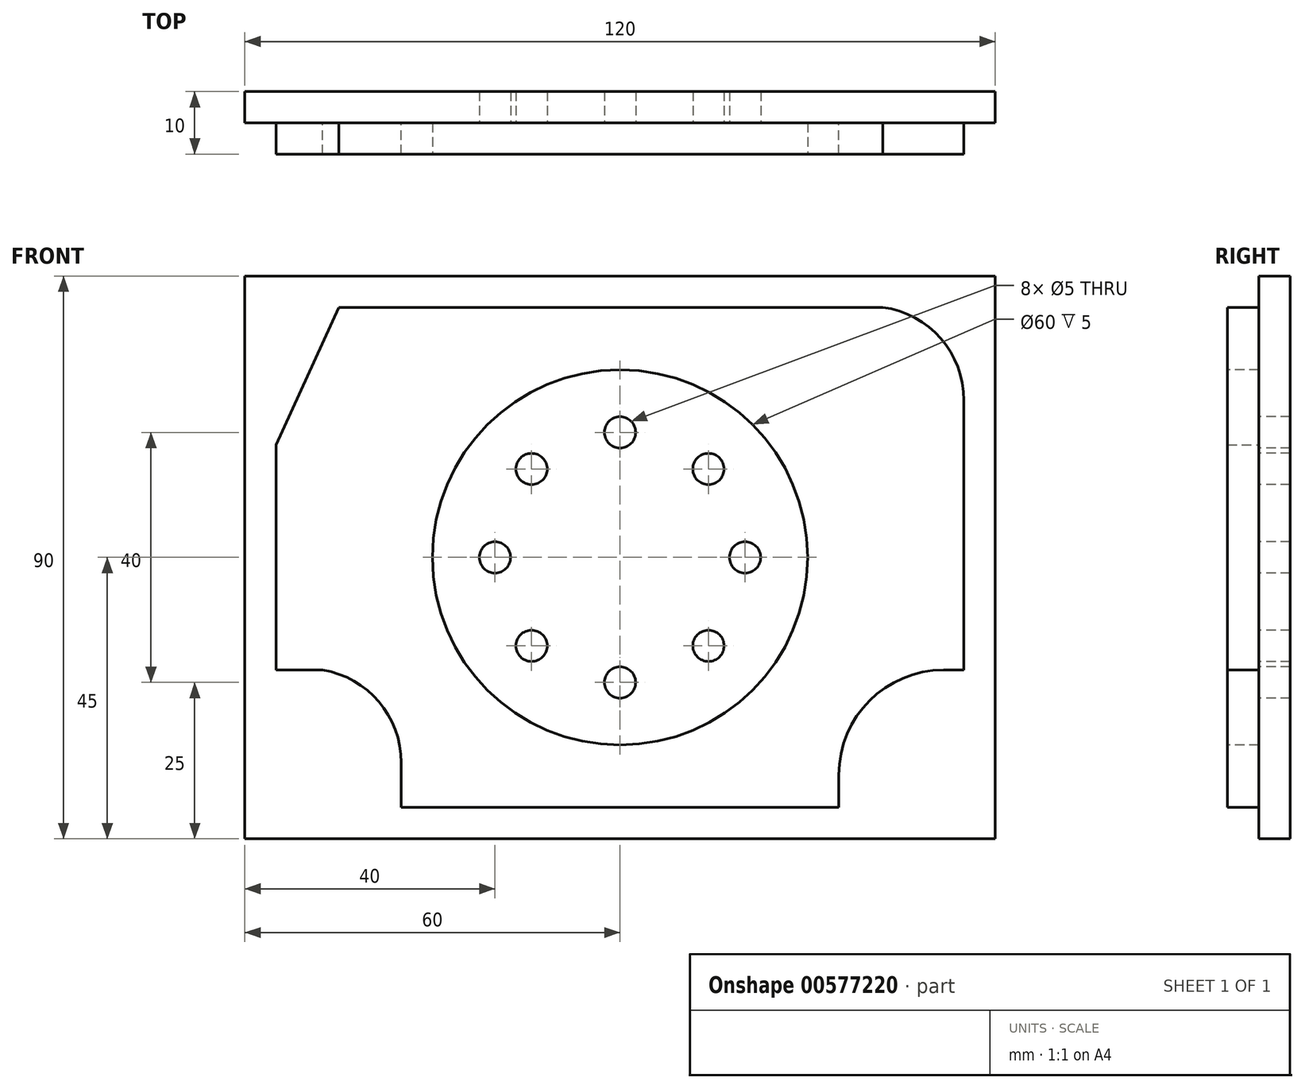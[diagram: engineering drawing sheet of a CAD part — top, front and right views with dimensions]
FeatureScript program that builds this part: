
annotation { "Feature Type Name" : "Feature", "Feature Type Description" : "" }
export const myFeature = defineFeature(function(context is Context, id is Id, definition is map)
    precondition{}
    {
        {
            var Q0;
            Q0=qCreatedBy(makeId("Front.planeOp"),FACE);
            var sketch = newSketch(context, id + "F0", { "sketchPlane" : qUnion([Q0])});
            skLineSegment(sketch, "E0.bottom", {"start": v(0, 0) * mm, "end": v(-120, 0) * mm});
            skLineSegment(sketch, "E0.top", {"start": v(0, 90) * mm, "end": v(-120, 90) * mm});
            skLineSegment(sketch, "E0.left", {"start": v(0, 0) * mm, "end": v(0, 90) * mm});
            skLineSegment(sketch, "E0.right", {"start": v(-120, 0) * mm, "end": v(-120, 90) * mm});
            skSolve(sketch);
        }
        {
            var Q0;
            Q0=makeQuery(id+"F0.imprint","IMPRINT",FACE,{"disambiguationData":[TD([[makeQuery(id+"F0.imprint","IMPRINT",EDGE,{"derivedFrom":sQuery(id+"F0.wireOp",EDGE,"E0.bottom")}),-1.0]])]});
            extrude(context, id + "F1", {"entities" : qUnion([Q0]), "depth" : 5 * mm, "offsetDistance" : 25 * mm});
        }
        {
            var Q0;
            Q0=makeQuery(id+"F1.opExtrude","CAP_FACE",FACE,{"disambiguationData":[OSD([sQuery(id+"F0.wireOp",EDGE,"E0.bottom"),sQuery(id+"F0.wireOp",EDGE,"E0.top"),sQuery(id+"F0.wireOp",EDGE,"E0.left"),sQuery(id+"F0.wireOp",EDGE,"E0.right")])],"isStart":false});
            var sketch = newSketch(context, id + "F2", { "sketchPlane" : qUnion([Q0])});
            skCircle(sketch, "E1", {"center": v(-60, 45) * mm, "radius": 20 * mm, "construction": true});
            skCircle(sketch, "E2", {"center": v(-60, 65) * mm, "radius": 3 * mm});
            skCircle(sketch, "E3", {"center": v(-60, 25) * mm, "radius": 3 * mm});
            skCircle(sketch, "E4", {"center": v(-45.86, 59.14) * mm, "radius": 3 * mm});
            skCircle(sketch, "E5", {"center": v(-45.86, 30.86) * mm, "radius": 3 * mm});
            skCircle(sketch, "E6", {"center": v(-74.14, 30.86) * mm, "radius": 3 * mm});
            skCircle(sketch, "E7", {"center": v(-74.14, 59.14) * mm, "radius": 3 * mm});
            skCircle(sketch, "E8", {"center": v(-80, 45) * mm, "radius": 3 * mm});
            skCircle(sketch, "E9", {"center": v(-40, 45) * mm, "radius": 3 * mm});
            skSolve(sketch);
        }
        {
            var Q0;
            Q0=sQuery(id+"F2.wireOp",VERTEX,"E7.center");
            var Q1;
            Q1=sQuery(id+"F2.wireOp",VERTEX,"E2.center");
            var Q2;
            Q2=sQuery(id+"F2.wireOp",VERTEX,"E4.center");
            var Q3;
            Q3=sQuery(id+"F2.wireOp",VERTEX,"E9.center");
            var Q4;
            Q4=sQuery(id+"F2.wireOp",VERTEX,"E5.center");
            var Q5;
            Q5=sQuery(id+"F2.wireOp",VERTEX,"E3.center");
            var Q6;
            Q6=sQuery(id+"F2.wireOp",VERTEX,"E8.center");
            var Q7;
            Q7=sQuery(id+"F2.wireOp",VERTEX,"E6.center");
            var Q8;
            Q8=makeQuery(id+"F1.opExtrude","SWEPT_BODY",BODY,{"disambiguationData":[OSD([sQuery(id+"F0.wireOp",EDGE,"E0.bottom"),sQuery(id+"F0.wireOp",EDGE,"E0.top"),sQuery(id+"F0.wireOp",EDGE,"E0.left"),sQuery(id+"F0.wireOp",EDGE,"E0.right")])]});
            hole(context, id + "F3", {"style" : HoleStyle.SIMPLE, "endStyle" : HoleEndStyle.THROUGH, "holeDiameter" : 5 * mm, "isTappedThrough" : true, "tappedDepth" : 12 * mm, "tapClearance" : 3, "locations" : qUnion([Q0, Q1, Q2, Q3, Q4, Q5, Q6, Q7]), "scope" : qUnion([Q8])});
        }
        {
            var Q0;
            Q0=makeQuery(id+"F1.opExtrude","CAP_FACE",FACE,{"disambiguationData":[OSD([sQuery(id+"F0.wireOp",EDGE,"E0.bottom"),sQuery(id+"F0.wireOp",EDGE,"E0.top"),sQuery(id+"F0.wireOp",EDGE,"E0.left"),sQuery(id+"F0.wireOp",EDGE,"E0.right")])],"isStart":false});
            var sketch = newSketch(context, id + "F4", { "sketchPlane" : qUnion([Q0])});
            skLineSegment(sketch, "E10", {"start": v(-5, 70.14) * mm, "end": v(-5, 27) * mm});
            skArc(sketch, "E11", {"start": v(-5, 70.14) * mm, "mid": v(-8.7, 80) * mm, "end": v(-17.99, 85) * mm});
            skLineSegment(sketch, "E12", {"start": v(-95, 5) * mm, "end": v(-25, 5) * mm});
            skLineSegment(sketch, "E13", {"start": v(-5, 27) * mm, "end": v(-8.23, 27) * mm});
            skLineSegment(sketch, "E14", {"start": v(-25, 5) * mm, "end": v(-25, 10.23) * mm});
            skLineSegment(sketch, "E15", {"start": v(-5, 27) * mm, "end": v(-5, 5) * mm, "construction": true});
            skLineSegment(sketch, "E16", {"start": v(-5, 5) * mm, "end": v(-25, 5) * mm, "construction": true});
            skArc(sketch, "E17", {"start": v(-8.23, 27) * mm, "mid": v(-20.09, 22.09) * mm, "end": v(-25, 10.23) * mm});
            skLineSegment(sketch, "E18", {"start": v(-17.99, 85) * mm, "end": v(-105, 85) * mm});
            skLineSegment(sketch, "E19", {"start": v(-105, 85) * mm, "end": v(-115, 63) * mm});
            skLineSegment(sketch, "E20", {"start": v(-115, 63) * mm, "end": v(-115, 27) * mm});
            skLineSegment(sketch, "E21", {"start": v(-95, 5) * mm, "end": v(-95, 12.2) * mm});
            skLineSegment(sketch, "E22", {"start": v(-115, 27) * mm, "end": v(-107.58, 27) * mm});
            skArc(sketch, "E23", {"start": v(-95, 12.2) * mm, "mid": v(-98.57, 21.91) * mm, "end": v(-107.58, 27) * mm});
            skSolve(sketch);
        }
        {
            var Q0;
            Q0=makeQuery(id+"F4.imprint","IMPRINT",FACE,{"disambiguationData":[TD([[makeQuery(id+"F4.imprint","IMPRINT",EDGE,{"derivedFrom":sQuery(id+"F4.wireOp",EDGE,"E10")}),-1.0]])]});
            extrude(context, id + "F5", {"entities" : qUnion([Q0]), "operationType" : NewBodyOperationType.ADD, "depth" : 5 * mm, "offsetDistance" : 25 * mm});
        }
        {
            var Q0;
            Q0=makeQuery(id+"F5.opExtrude","CAP_FACE",FACE,{"disambiguationData":[OSD([sQuery(id+"F3.hole-0.sketch.wireOp",EDGE,"core_line_2"),sQuery(id+"F3.hole-0.sketch.wireOp",EDGE,"core_line_3"),sQuery(id+"F3.hole-1.sketch.wireOp",EDGE,"core_line_2"),sQuery(id+"F3.hole-1.sketch.wireOp",EDGE,"core_line_3"),sQuery(id+"F3.hole-2.sketch.wireOp",EDGE,"core_line_2"),sQuery(id+"F3.hole-2.sketch.wireOp",EDGE,"core_line_3"),sQuery(id+"F3.hole-3.sketch.wireOp",EDGE,"core_line_2"),sQuery(id+"F3.hole-3.sketch.wireOp",EDGE,"core_line_3"),sQuery(id+"F3.hole-4.sketch.wireOp",EDGE,"core_line_2"),sQuery(id+"F3.hole-4.sketch.wireOp",EDGE,"core_line_3"),sQuery(id+"F3.hole-5.sketch.wireOp",EDGE,"core_line_2"),sQuery(id+"F3.hole-5.sketch.wireOp",EDGE,"core_line_3"),sQuery(id+"F3.hole-6.sketch.wireOp",EDGE,"core_line_2"),sQuery(id+"F3.hole-6.sketch.wireOp",EDGE,"core_line_3"),sQuery(id+"F3.hole-7.sketch.wireOp",EDGE,"core_line_2"),sQuery(id+"F3.hole-7.sketch.wireOp",EDGE,"core_line_3"),sQuery(id+"F4.wireOp",EDGE,"E10"),sQuery(id+"F4.wireOp",EDGE,"E11"),sQuery(id+"F4.wireOp",EDGE,"E12"),sQuery(id+"F4.wireOp",EDGE,"E13"),sQuery(id+"F4.wireOp",EDGE,"E14"),sQuery(id+"F4.wireOp",EDGE,"E17"),sQuery(id+"F4.wireOp",EDGE,"E18"),sQuery(id+"F4.wireOp",EDGE,"E19"),sQuery(id+"F4.wireOp",EDGE,"E20"),sQuery(id+"F4.wireOp",EDGE,"E21"),sQuery(id+"F4.wireOp",EDGE,"E22"),sQuery(id+"F4.wireOp",EDGE,"E23")])],"isStart":false});
            var sketch = newSketch(context, id + "F6", { "sketchPlane" : qUnion([Q0])});
            skCircle(sketch, "E24", {"center": v(-60, 45) * mm, "radius": 30 * mm});
            skSolve(sketch);
        }
        {
            var Q0;
            Q0=makeQuery(id+"F6.imprint","IMPRINT",FACE,{"disambiguationData":[TD([[makeQuery(id+"F6.imprint","IMPRINT",EDGE,{"derivedFrom":sQuery(id+"F6.wireOp",EDGE,"E24")}),1.0]])]});
            extrude(context, id + "F7", {"entities" : qUnion([Q0]), "operationType" : NewBodyOperationType.REMOVE, "oppositeDirection" : true, "depth" : 5 * mm, "offsetDistance" : 25 * mm});
        }
    });
